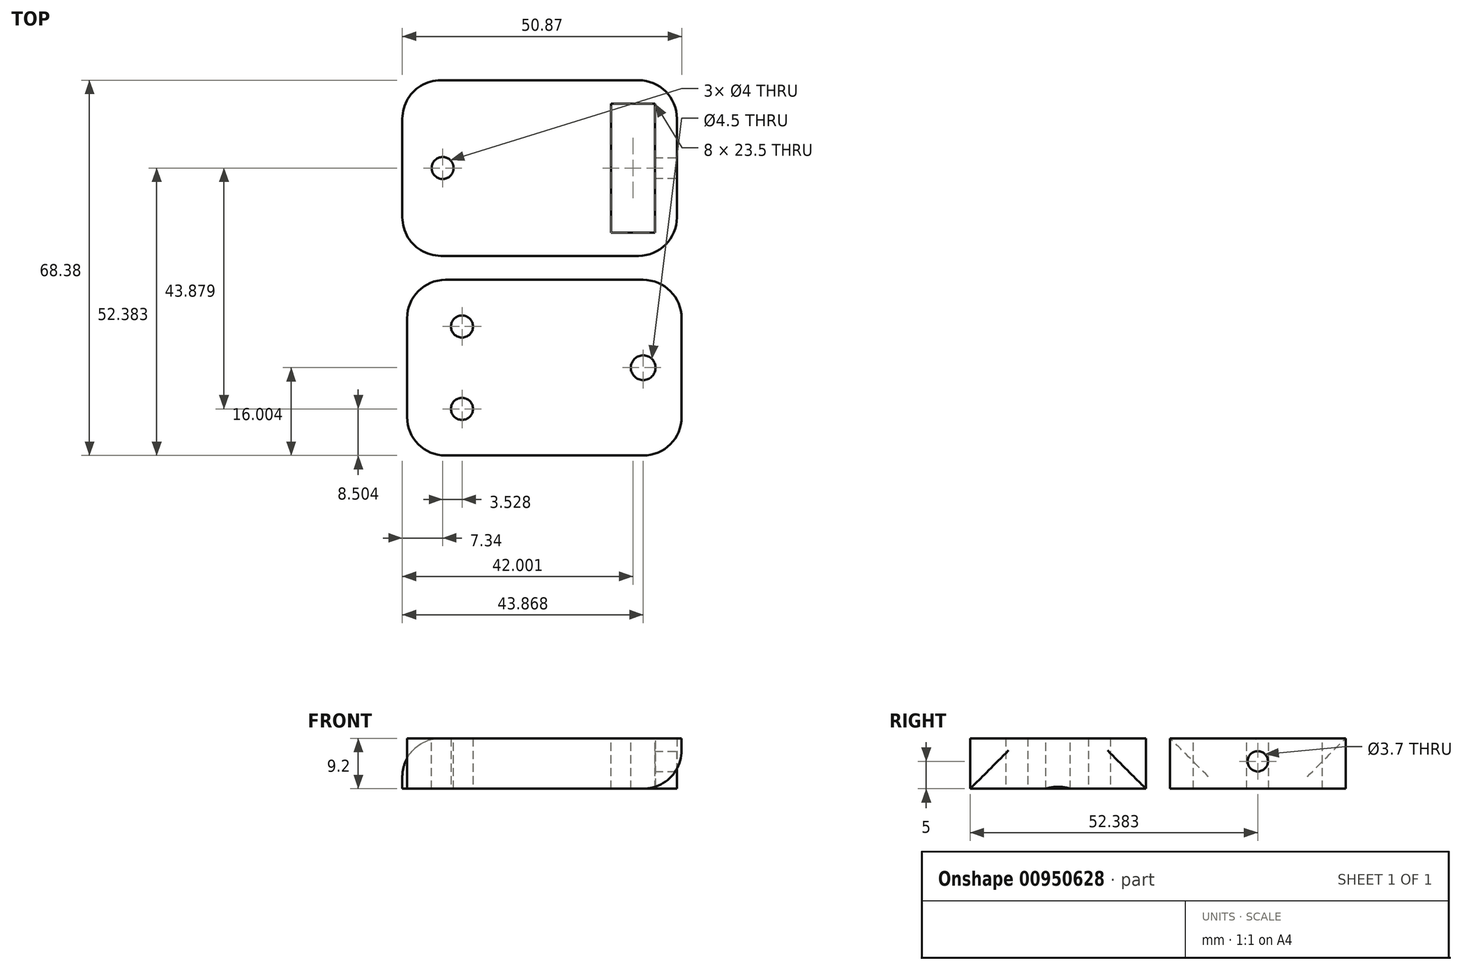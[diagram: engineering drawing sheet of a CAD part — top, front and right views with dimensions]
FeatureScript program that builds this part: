
annotation { "Feature Type Name" : "Feature", "Feature Type Description" : "" }
export const myFeature = defineFeature(function(context is Context, id is Id, definition is map)
    precondition{}
    {
        {
            var Q0;
            Q0=qCreatedBy(makeId("Top.planeOp"),FACE);
            var sketch = newSketch(context, id + "F0", { "sketchPlane" : qUnion([Q0])});
            skLineSegment(sketch, "E0.bottom", {"start": v(-31.96, 15.02) * mm, "end": v(18.04, 15.02) * mm});
            skLineSegment(sketch, "E0.top", {"start": v(-31.96, -16.98) * mm, "end": v(18.04, -16.98) * mm});
            skLineSegment(sketch, "E0.left", {"start": v(-31.96, 15.02) * mm, "end": v(-31.96, -16.98) * mm});
            skLineSegment(sketch, "E0.right", {"start": v(18.04, 15.02) * mm, "end": v(18.04, -16.98) * mm});
            skLineSegment(sketch, "E1.bottom", {"start": v(18.9, -53.36) * mm, "end": v(-31.1, -53.36) * mm});
            skLineSegment(sketch, "E1.top", {"start": v(18.9, -21.36) * mm, "end": v(-31.1, -21.36) * mm});
            skLineSegment(sketch, "E1.left", {"start": v(18.9, -53.36) * mm, "end": v(18.9, -21.36) * mm});
            skLineSegment(sketch, "E1.right", {"start": v(-31.1, -53.36) * mm, "end": v(-31.1, -21.36) * mm});
            skCircle(sketch, "E2", {"center": v(-21.1, -44.86) * mm, "radius": 2 * mm});
            skCircle(sketch, "E3", {"center": v(-21.1, -29.86) * mm, "radius": 2 * mm});
            skSolve(sketch);
        }
        {
            var Q0;
            Q0 = qSketchRegion(id + "F0", true);
            extrude(context, id + "F1", {"entities" : qUnion([Q0]), "depth" : 9.2 * mm, "offsetDistance" : 25 * mm});
        }
        {
            var Q0;
            Q0=makeQuery(id+"F1.opExtrude","CAP_FACE",FACE,{"disambiguationData":[OSD([sQuery(id+"F0.wireOp",EDGE,"E0.bottom"),sQuery(id+"F0.wireOp",EDGE,"E0.top"),sQuery(id+"F0.wireOp",EDGE,"E0.left"),sQuery(id+"F0.wireOp",EDGE,"E0.right")])],"isStart":false});
            var sketch = newSketch(context, id + "F2", { "sketchPlane" : qUnion([Q0])});
            skLineSegment(sketch, "E4.bottom", {"start": v(6.04, 10.77) * mm, "end": v(14.04, 10.77) * mm});
            skLineSegment(sketch, "E4.top", {"start": v(6.04, -12.73) * mm, "end": v(14.04, -12.73) * mm});
            skLineSegment(sketch, "E4.left", {"start": v(6.04, 10.77) * mm, "end": v(6.04, -12.73) * mm});
            skLineSegment(sketch, "E4.right", {"start": v(14.04, 10.77) * mm, "end": v(14.04, -12.73) * mm});
            skCircle(sketch, "E5", {"center": v(-24.62, -0.98) * mm, "radius": 2 * mm});
            skSolve(sketch);
        }
        {
            var Q0;
            Q0=makeQuery(id+"F2.imprint","IMPRINT",FACE,{"disambiguationData":[TD([[makeQuery(id+"F2.imprint","IMPRINT",EDGE,{"derivedFrom":sQuery(id+"F2.wireOp",EDGE,"E4.bottom")}),-1.0]])]});
            var Q1;
            Q1=makeQuery(id+"F2.imprint","IMPRINT",FACE,{"disambiguationData":[TD([[makeQuery(id+"F2.imprint","IMPRINT",EDGE,{"derivedFrom":sQuery(id+"F2.wireOp",EDGE,"NCds5BFH-t4Id-2zwf-doRS-KX9CpPjDlQgJ")}),1.0]])]});
            var Q2;
            Q2=makeQuery(id+"F2.imprint","IMPRINT",FACE,{"disambiguationData":[TD([[makeQuery(id+"F2.imprint","IMPRINT",EDGE,{"derivedFrom":sQuery(id+"F2.wireOp",EDGE,"avfTDBd6-kbh5-bCmk-vPd7-ydhfcEMmiGgP")}),1.0]])]});
            var Q3;
            Q3=makeQuery(id+"F2.imprint","IMPRINT",FACE,{"disambiguationData":[TD([[makeQuery(id+"F2.imprint","IMPRINT",EDGE,{"derivedFrom":sQuery(id+"F2.wireOp",EDGE,"E5")}),1.0]])]});
            extrude(context, id + "F3", {"entities" : qUnion([Q0, Q1, Q2, Q3]), "operationType" : NewBodyOperationType.REMOVE, "oppositeDirection" : true, "depth" : 25 * mm, "offsetDistance" : 25 * mm});
        }
        {
            var Q0;
            Q0=makeQuery(id+"F1.opExtrude","SWEPT_FACE",FACE,{"disambiguationData":[OSD([sQuery(id+"F0.wireOp",EDGE,"E0.right")])]});
            var sketch = newSketch(context, id + "F4", { "sketchPlane" : qUnion([Q0])});
            skCircle(sketch, "E6", {"center": v(-0.98, 5) * mm, "radius": 1.85 * mm});
            skSolve(sketch);
        }
        {
            var Q0;
            Q0 = qSketchRegion(id + "F4", true);
            var Q1;
            Q1=makeQuery(id+"F4.imprint","IMPRINT",FACE,{"disambiguationData":[TD([[makeQuery(id+"F4.imprint","IMPRINT",EDGE,{"derivedFrom":sQuery(id+"F4.wireOp",EDGE,"E6")}),1.0]])]});
            extrude(context, id + "F5", {"entities" : qUnion([Q0, Q1]), "operationType" : NewBodyOperationType.REMOVE, "oppositeDirection" : true, "depth" : 5 * mm, "offsetDistance" : 25 * mm});
        }
        {
            var Q0;
            Q0=makeQuery(id+"F1.opExtrude","CAP_FACE",FACE,{"disambiguationData":[OSD([sQuery(id+"F0.wireOp",EDGE,"E1.bottom"),sQuery(id+"F0.wireOp",EDGE,"E1.top"),sQuery(id+"F0.wireOp",EDGE,"E1.left"),sQuery(id+"F0.wireOp",EDGE,"E1.right"),sQuery(id+"F0.wireOp",EDGE,"E2"),sQuery(id+"F0.wireOp",EDGE,"E3")])],"isStart":false});
            var sketch = newSketch(context, id + "F6", { "sketchPlane" : qUnion([Q0])});
            skCircle(sketch, "E7", {"center": v(11.9, -37.36) * mm, "radius": 2.25 * mm});
            skSolve(sketch);
        }
        {
            var Q0;
            Q0=makeQuery(id+"F6.imprint","IMPRINT",FACE,{"disambiguationData":[TD([[makeQuery(id+"F6.imprint","IMPRINT",EDGE,{"derivedFrom":sQuery(id+"F6.wireOp",EDGE,"E7")}),1.0]])]});
            extrude(context, id + "F7", {"entities" : qUnion([Q0]), "operationType" : NewBodyOperationType.REMOVE, "oppositeDirection" : true, "depth" : 25 * mm, "offsetDistance" : 25 * mm});
        }
        {
            var Q0;
            Q0=makeQuery(id+"F1.opExtrude","SWEPT_EDGE",EDGE,{"disambiguationData":[OSD([sQuery(id+"F0.wireOp",EDGE,"E1.top"),sQuery(id+"F0.wireOp",EDGE,"E1.left")])]});
            var Q1;
            Q1=makeQuery(id+"F1.opExtrude","SWEPT_EDGE",EDGE,{"disambiguationData":[OSD([sQuery(id+"F0.wireOp",EDGE,"E1.bottom"),sQuery(id+"F0.wireOp",EDGE,"E1.left")])]});
            var Q2;
            Q2=makeQuery(id+"F1.opExtrude","CAP_EDGE",EDGE,{"disambiguationData":[OSD([sQuery(id+"F0.wireOp",EDGE,"E1.left")])],"isStart":true});
            var Q3;
            Q3=makeQuery(id+"F1.opExtrude","CAP_EDGE",EDGE,{"disambiguationData":[OSD([sQuery(id+"F0.wireOp",EDGE,"E0.left")])],"isStart":false});
            var Q4;
            Q4=makeQuery(id+"F1.opExtrude","SWEPT_EDGE",EDGE,{"disambiguationData":[OSD([sQuery(id+"F0.wireOp",EDGE,"E0.top"),sQuery(id+"F0.wireOp",EDGE,"E0.left")])]});
            var Q5;
            Q5=makeQuery(id+"F1.opExtrude","SWEPT_EDGE",EDGE,{"disambiguationData":[OSD([sQuery(id+"F0.wireOp",EDGE,"E0.bottom"),sQuery(id+"F0.wireOp",EDGE,"E0.left")])]});
            var Q6;
            Q6=makeQuery(id+"F1.opExtrude","SWEPT_EDGE",EDGE,{"disambiguationData":[OSD([sQuery(id+"F0.wireOp",EDGE,"E1.bottom"),sQuery(id+"F0.wireOp",EDGE,"E1.right")])]});
            var Q7;
            Q7=makeQuery(id+"F1.opExtrude","SWEPT_EDGE",EDGE,{"disambiguationData":[OSD([sQuery(id+"F0.wireOp",EDGE,"E1.top"),sQuery(id+"F0.wireOp",EDGE,"E1.right")])]});
            var Q8;
            Q8=makeQuery(id+"F1.opExtrude","SWEPT_EDGE",EDGE,{"disambiguationData":[OSD([sQuery(id+"F0.wireOp",EDGE,"E0.top"),sQuery(id+"F0.wireOp",EDGE,"E0.right")])]});
            var Q9;
            Q9=makeQuery(id+"F1.opExtrude","SWEPT_EDGE",EDGE,{"disambiguationData":[OSD([sQuery(id+"F0.wireOp",EDGE,"E0.bottom"),sQuery(id+"F0.wireOp",EDGE,"E0.right")])]});
            fillet(context, id + "F8", {"entities" : qUnion([Q0, Q1, Q2, Q3, Q4, Q5, Q6, Q7, Q8, Q9]), "tangentPropagation" : true, "radius" : 7 * mm, "defaultsChanged" : false, "vertexSettings" : [], "allowEdgeOverflow" : false});
        }
    });
